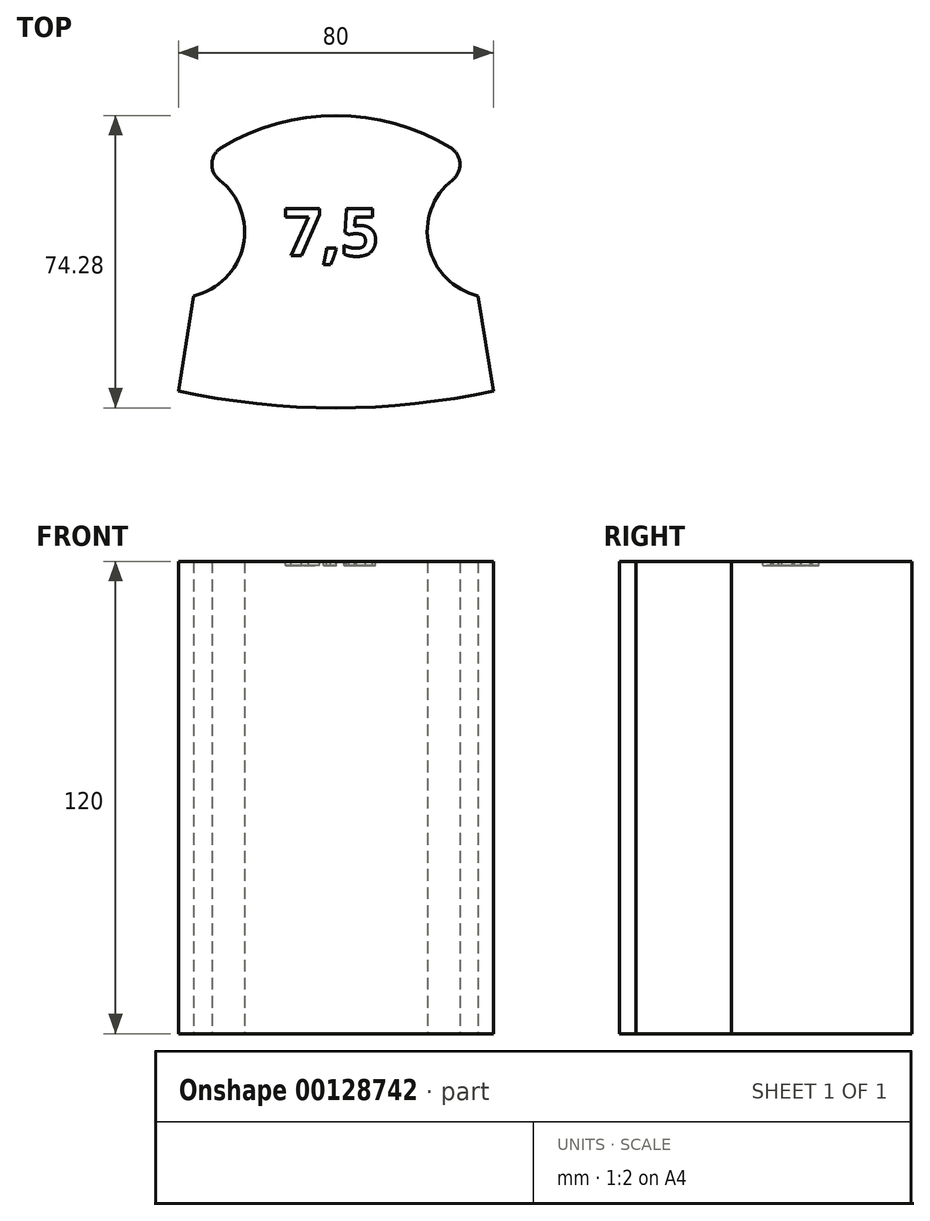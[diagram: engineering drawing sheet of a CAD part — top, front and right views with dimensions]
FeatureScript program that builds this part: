
annotation { "Feature Type Name" : "Feature", "Feature Type Description" : "" }
export const myFeature = defineFeature(function(context is Context, id is Id, definition is map)
    precondition{}
    {
        {
            var Q0;
            Q0=qCreatedBy(makeId("Top.planeOp"),FACE);
            var sketch = newSketch(context, id + "F0", { "sketchPlane" : qUnion([Q0])});
            skLineSegment(sketch, "E0", {"start": v(0, 0) * mm, "end": v(3.87, 24.16) * mm});
            skLineSegment(sketch, "E1", {"start": v(0, 0) * mm, "end": v(80, 0) * mm, "construction": true});
            skLineSegment(sketch, "E2", {"start": v(40, 0) * mm, "end": v(40, 70) * mm, "construction": true});
            skArc(sketch, "E3", {"start": v(3.87, 24.16) * mm, "mid": v(16.4, 36.85) * mm, "end": v(10.4, 53.64) * mm});
            skArc(sketch, "E4.MirrorCS", {"start": v(76.13, 24.16) * mm, "mid": v(63.6, 36.85) * mm, "end": v(69.6, 53.64) * mm});
            skLineSegment(sketch, "E5.MirrorCS", {"start": v(80, 0) * mm, "end": v(76.13, 24.16) * mm});
            skArc(sketch, "E6", {"start": v(69.1, 61.84) * mm, "mid": v(40, 70) * mm, "end": v(10.9, 61.84) * mm});
            skPoint(sketch, "E7.visualSharp", {"position": v(3.87, 56.79) * mm});
            skArc(sketch, "E7.filletArc", {"start": v(10.9, 61.84) * mm, "mid": v(8.5, 57.87) * mm, "end": v(10.4, 53.64) * mm});
            skPoint(sketch, "E8.visualSharp", {"position": v(76.13, 56.79) * mm});
            skArc(sketch, "E8.filletArc", {"start": v(69.6, 53.64) * mm, "mid": v(71.5, 57.87) * mm, "end": v(69.1, 61.84) * mm});
            skArc(sketch, "E9", {"start": v(0, 0) * mm, "mid": v(40, -4.28) * mm, "end": v(80, 0) * mm});
            skSolve(sketch);
        }
        {
            var Q0;
            Q0=makeQuery(id+"F0.imprint","IMPRINT",FACE,{"disambiguationData":[TD([[makeQuery(id+"F0.imprint","IMPRINT",EDGE,{"derivedFrom":sQuery(id+"F0.wireOp",EDGE,"E0")}),-1.0]])]});
            extrude(context, id + "F1", {"entities" : qUnion([Q0]), "depth" : 120 * mm});
        }
        {
            var Q0;
            Q0=makeQuery(id+"F1.opExtrude","CAP_FACE",FACE,{"disambiguationData":[OSD([sQuery(id+"F0.wireOp",EDGE,"E0"),sQuery(id+"F0.wireOp",EDGE,"E3"),sQuery(id+"F0.wireOp",EDGE,"E4.MirrorCS"),sQuery(id+"F0.wireOp",EDGE,"E5.MirrorCS"),sQuery(id+"F0.wireOp",EDGE,"E6"),sQuery(id+"F0.wireOp",EDGE,"E7.filletArc"),sQuery(id+"F0.wireOp",EDGE,"E8.filletArc"),sQuery(id+"F0.wireOp",EDGE,"E9")])],"isStart":false});
            var sketch = newSketch(context, id + "F2", { "sketchPlane" : qUnion([Q0])});
            skText(sketch, "E10", { "text": "7,5", "fontName": "OpenSans-Bold.ttf"});
            skPoint(sketch, "E11", {"position": v(40, 70) * mm});
            const initialGuessF2  = {"E10": [0.02669, 0.03435, 1, 0, 0.01214]};
            skSetInitialGuess(sketch, initialGuessF2);
            skSolve(sketch);
        }
        {
            var Q0;
            Q0 = qSketchRegion(id + "F2", true);
            extrude(context, id + "F3", {"entities" : qUnion([Q0]), "operationType" : NewBodyOperationType.REMOVE, "oppositeDirection" : true, "depth" : 1 * mm});
        }
    });
